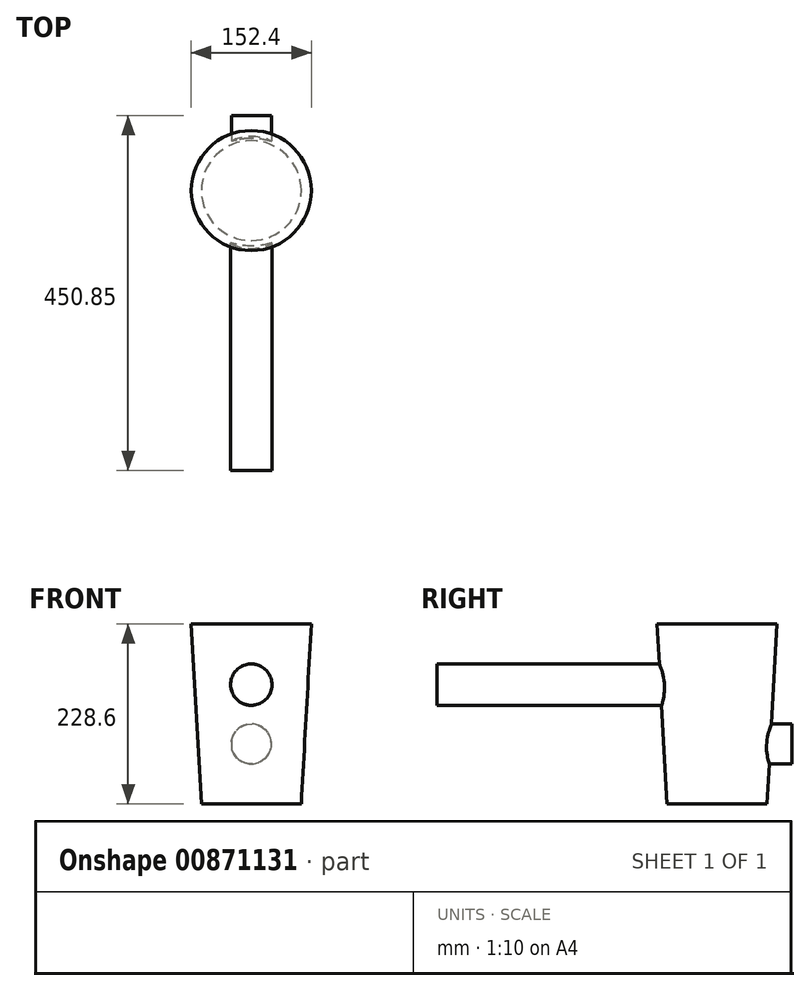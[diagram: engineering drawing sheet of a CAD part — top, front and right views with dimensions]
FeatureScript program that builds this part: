
annotation { "Feature Type Name" : "Feature", "Feature Type Description" : "" }
export const myFeature = defineFeature(function(context is Context, id is Id, definition is map)
    precondition{}
    {
        {
            var Q0;
            Q0=qCreatedBy(makeId("Top.planeOp"),FACE);
            cPlane(context, id + "F0", {"entities" : qUnion([Q0]), "cplaneType" : CPlaneType.OFFSET, "offset" : 228.6 * mm, "width" : 152.4 * mm, "height" : 152.4 * mm});
        }
        {
            var Q0;
            Q0=qCreatedBy(makeId("Top.planeOp"),FACE);
            var sketch = newSketch(context, id + "F1", { "sketchPlane" : qUnion([Q0])});
            skCircle(sketch, "E0", {"center": v(0, 0) * mm, "radius": 63.5 * mm});
            skSolve(sketch);
        }
        {
            var Q0;
            Q0=qCreatedBy(id+"F0.planeOp",FACE);
            var sketch = newSketch(context, id + "F2", { "sketchPlane" : qUnion([Q0])});
            skCircle(sketch, "E1", {"center": v(0, 0) * mm, "radius": 76.2 * mm});
            skSolve(sketch);
        }
        {
            var Q0;
            Q0=makeQuery(id+"F1.imprint","IMPRINT",FACE,{"disambiguationData":[TD([[makeQuery(id+"F1.imprint","IMPRINT",EDGE,{"derivedFrom":sQuery(id+"F1.wireOp",EDGE,"E0")}),1.0]])]});
            var Q1;
            Q1=makeQuery(id+"F2.imprint","IMPRINT",FACE,{"disambiguationData":[TD([[makeQuery(id+"F2.imprint","IMPRINT",EDGE,{"derivedFrom":sQuery(id+"F2.wireOp",EDGE,"E1")}),1.0]])]});
            loft(context, id + "F3", {"sheetProfilesArray" : [{ "sheetProfileEntities" : qUnion([Q0]) }, { "sheetProfileEntities" : qUnion([Q1]) }]});
        }
        {
            var Q0;
            Q0=qCreatedBy(makeId("Front.planeOp"),FACE);
            var sketch = newSketch(context, id + "F4", { "sketchPlane" : qUnion([Q0])});
            skCircle(sketch, "E2", {"center": v(0, 151.55) * mm, "radius": 26.25 * mm});
            skSolve(sketch);
        }
        {
            var Q0;
            Q0 = qSketchRegion(id + "F4", true);
            extrude(context, id + "F5", {"entities" : qUnion([Q0]), "operationType" : NewBodyOperationType.ADD, "depth" : 355.6 * mm, "offsetDistance" : 25.4 * mm});
        }
        {
            var Q0;
            Q0=qCreatedBy(makeId("Front.planeOp"),FACE);
            var sketch = newSketch(context, id + "F6", { "sketchPlane" : qUnion([Q0])});
            skCircle(sketch, "E3", {"center": v(0, 76.2) * mm, "radius": 25.4 * mm});
            skSolve(sketch);
        }
        {
            var Q0;
            Q0 = qSketchRegion(id + "F6", true);
            extrude(context, id + "F7", {"entities" : qUnion([Q0]), "operationType" : NewBodyOperationType.ADD, "oppositeDirection" : true, "depth" : 95.25 * mm, "offsetDistance" : 25.4 * mm});
        }
    });
